# Revit family: Haworth_Masters_Convergent_TDesk
name_source: partatom
category: Furniture Systems
revit_build: Autodesk Revit 2018 (Build: 20170223_1515(x64)
units: mm (PartAtom-declared; Revit-internal decimal feet)

## family parameters
Always vertical = Yes
Cut with Voids When Loaded = No
OmniClass Number = 23.40.70.14.64.21
OmniClass Title = Systems Furniture
Part Type = Normal
Room Calculation Point = No
Round Connector Dimension = Use Diameter
Shared = No
Work Plane-Based = No

## types (2) — shared parameters
Actual Height = 29 1/8"
Assembly Code = E2020200
Cabinet Finish = Haworth _ Wood _ White Oak
Custom Size = No
Description = Haworth - Masters - Convergent T-Desk
Edge Finish = Haworth _ Wood _ White Oak
Manufacturer = Haworth
Max. Depth = 36"
Max. Width = 78"
Min. Depth = 30"
Min. Width = 48"
Model = Haworth - Masters - Convergent T-Desk
Revision Number = 2
Size = Verify Final Dim. w/ Haworth
Standard Depths = 30, 36 in.
Standard Widths = 48,54,60,66,72,78 in.
Sustainability Info = http://www.haworth.com
URL = www.haworth.com
URL - Product = http://www.haworth.com
Warranty = http://www.haworth.com
Worksurface Finish = Haworth _ Wood _ White Oak

## per-type parameters (varying)
| type | Actual Depth | Actual Width | Depth | Width |
| 30d 48w | 30" | 48" | 30" | 48" |
| 36d 72w | 36" | 72" | 36" | 72" |

## geometry (parser evidence)
native form markers: Sweep x2
no freeform markers — native parametric forms only
